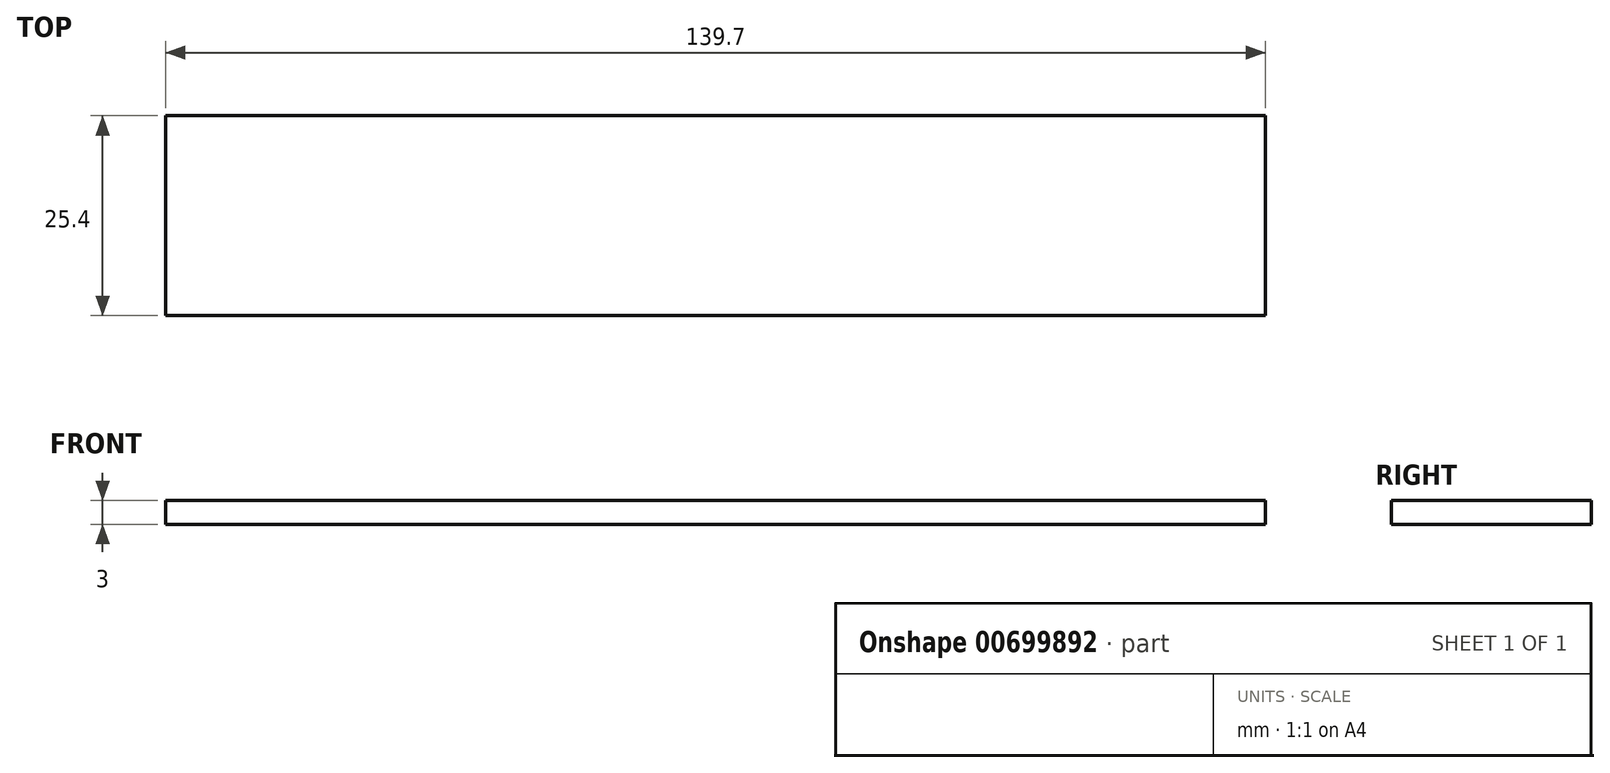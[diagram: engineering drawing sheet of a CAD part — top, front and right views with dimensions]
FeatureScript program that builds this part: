
annotation { "Feature Type Name" : "Feature", "Feature Type Description" : "" }
export const myFeature = defineFeature(function(context is Context, id is Id, definition is map)
    precondition{}
    {
        {
            var Q0;
            Q0=qCreatedBy(makeId("Top.planeOp"),FACE);
            var sketch = newSketch(context, id + "F0", { "sketchPlane" : qUnion([Q0])});
            skLineSegment(sketch, "E0.bottom", {"start": v(-69.85, 12.7) * mm, "end": v(69.85, 12.7) * mm});
            skLineSegment(sketch, "E0.top", {"start": v(-69.85, -12.7) * mm, "end": v(69.85, -12.7) * mm});
            skLineSegment(sketch, "E0.left", {"start": v(-69.85, 12.7) * mm, "end": v(-69.85, -12.7) * mm});
            skLineSegment(sketch, "E0.right", {"start": v(69.85, 12.7) * mm, "end": v(69.85, -12.7) * mm});
            skSolve(sketch);
        }
        {
            var Q0;
            Q0 = qSketchRegion(id + "F0", true);
            extrude(context, id + "F1", {"entities" : qUnion([Q0]), "depth" : 3 * mm, "offsetDistance" : 25.4 * mm});
        }
    });
